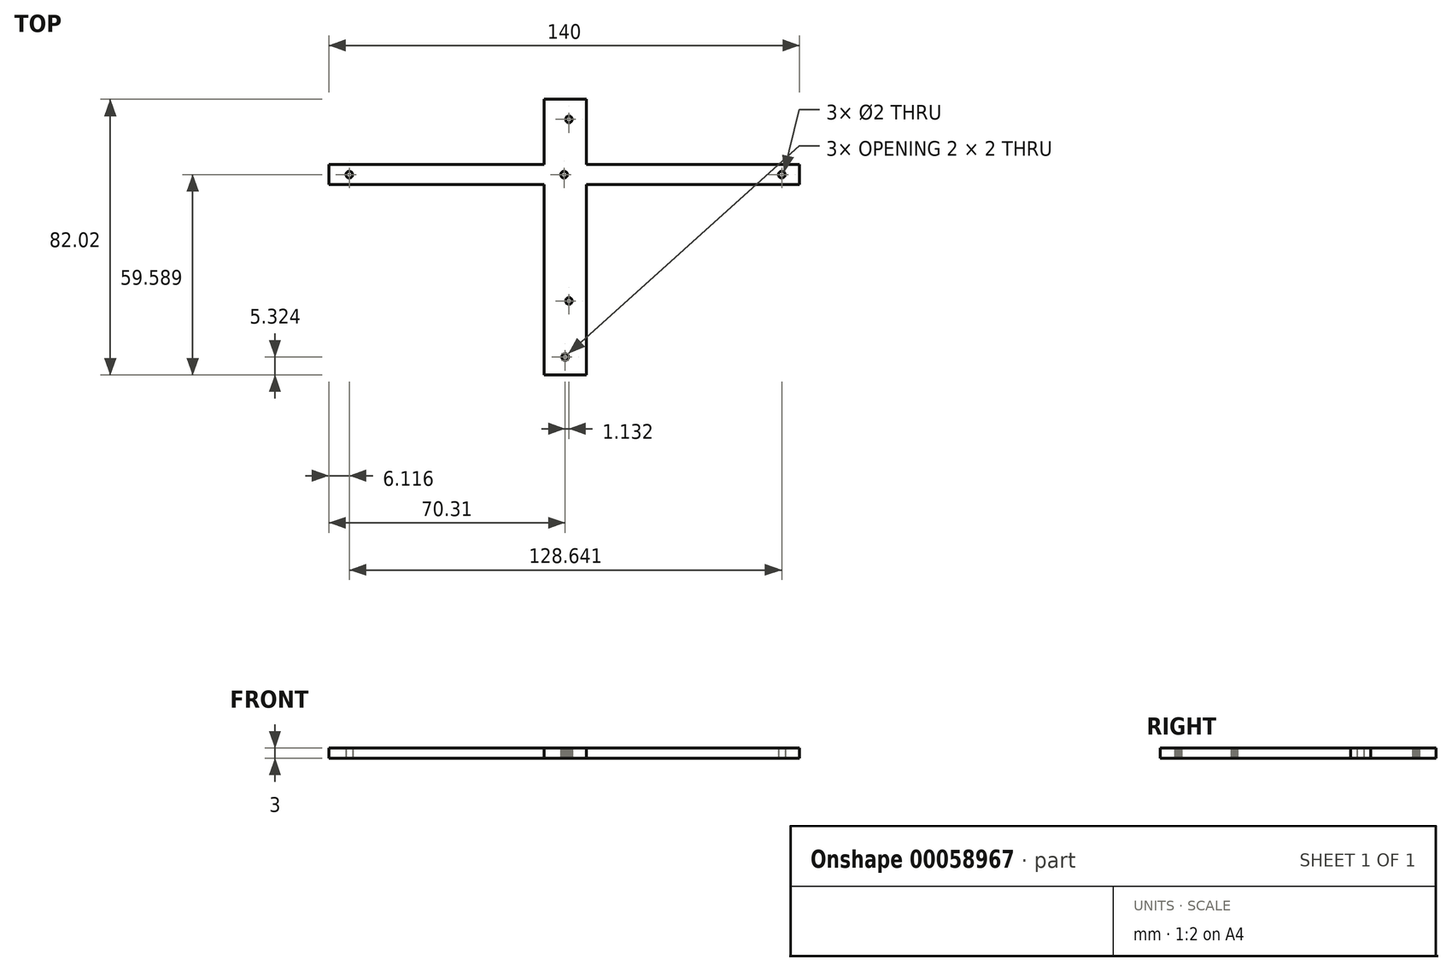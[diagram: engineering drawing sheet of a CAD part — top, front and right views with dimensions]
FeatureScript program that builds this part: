
annotation { "Feature Type Name" : "Feature", "Feature Type Description" : "" }
export const myFeature = defineFeature(function(context is Context, id is Id, definition is map)
    precondition{}
    {
        {
            var Q0;
            Q0=qCreatedBy(makeId("Top.planeOp"),FACE);
            var sketch = newSketch(context, id + "F0", { "sketchPlane" : qUnion([Q0])});
            skLineSegment(sketch, "E0", {"start": v(0.84, 33.8) * mm, "end": v(0.83, 33.92) * mm});
            skLineSegment(sketch, "E1", {"start": v(0.83, 33.92) * mm, "end": v(0.81, 34.04) * mm});
            skLineSegment(sketch, "E2", {"start": v(0.81, 34.04) * mm, "end": v(0.77, 34.16) * mm});
            skLineSegment(sketch, "E3", {"start": v(0.77, 34.16) * mm, "end": v(0.72, 34.28) * mm});
            skLineSegment(sketch, "E4", {"start": v(0.72, 34.28) * mm, "end": v(0.65, 34.38) * mm});
            skLineSegment(sketch, "E5", {"start": v(0.65, 34.38) * mm, "end": v(0.57, 34.48) * mm});
            skLineSegment(sketch, "E6", {"start": v(0.57, 34.48) * mm, "end": v(0.48, 34.57) * mm});
            skLineSegment(sketch, "E7", {"start": v(0.48, 34.57) * mm, "end": v(0.38, 34.64) * mm});
            skLineSegment(sketch, "E8", {"start": v(0.38, 34.64) * mm, "end": v(0.27, 34.7) * mm});
            skLineSegment(sketch, "E9", {"start": v(0.27, 34.7) * mm, "end": v(0.15, 34.75) * mm});
            skLineSegment(sketch, "E10", {"start": v(0.15, 34.75) * mm, "end": v(0.03, 34.78) * mm});
            skLineSegment(sketch, "E11", {"start": v(0.03, 34.78) * mm, "end": v(-0.1, 34.8) * mm});
            skLineSegment(sketch, "E12", {"start": v(-0.1, 34.8) * mm, "end": v(-0.22, 34.8) * mm});
            skLineSegment(sketch, "E13", {"start": v(-0.22, 34.8) * mm, "end": v(-0.35, 34.78) * mm});
            skLineSegment(sketch, "E14", {"start": v(-0.35, 34.78) * mm, "end": v(-0.47, 34.75) * mm});
            skLineSegment(sketch, "E15", {"start": v(-0.58, 34.7) * mm, "end": v(-0.7, 34.64) * mm});
            skLineSegment(sketch, "E16", {"start": v(-0.7, 34.64) * mm, "end": v(-0.8, 34.57) * mm});
            skLineSegment(sketch, "E17", {"start": v(-0.8, 34.57) * mm, "end": v(-0.89, 34.48) * mm});
            skLineSegment(sketch, "E18", {"start": v(-0.89, 34.48) * mm, "end": v(-0.97, 34.38) * mm});
            skLineSegment(sketch, "E19", {"start": v(-0.97, 34.38) * mm, "end": v(-1.03, 34.28) * mm});
            skLineSegment(sketch, "E20", {"start": v(-1.03, 34.28) * mm, "end": v(-1.09, 34.16) * mm});
            skLineSegment(sketch, "E21", {"start": v(-1.09, 34.16) * mm, "end": v(-1.13, 34.04) * mm});
            skLineSegment(sketch, "E22", {"start": v(-1.13, 34.04) * mm, "end": v(-1.15, 33.92) * mm});
            skLineSegment(sketch, "E23", {"start": v(-1.15, 33.92) * mm, "end": v(-1.16, 33.8) * mm});
            skLineSegment(sketch, "E24", {"start": v(-1.16, 33.8) * mm, "end": v(-1.15, 33.67) * mm});
            skLineSegment(sketch, "E25", {"start": v(-1.15, 33.67) * mm, "end": v(-1.13, 33.55) * mm});
            skLineSegment(sketch, "E26", {"start": v(-1.13, 33.55) * mm, "end": v(-1.09, 33.43) * mm});
            skLineSegment(sketch, "E27", {"start": v(-1.09, 33.43) * mm, "end": v(-1.03, 33.31) * mm});
            skLineSegment(sketch, "E28", {"start": v(-1.03, 33.31) * mm, "end": v(-0.97, 33.2) * mm});
            skLineSegment(sketch, "E29", {"start": v(-0.97, 33.2) * mm, "end": v(-0.89, 33.11) * mm});
            skLineSegment(sketch, "E30", {"start": v(-0.89, 33.11) * mm, "end": v(-0.8, 33.03) * mm});
            skLineSegment(sketch, "E31", {"start": v(-0.8, 33.03) * mm, "end": v(-0.7, 32.95) * mm});
            skLineSegment(sketch, "E32", {"start": v(-0.7, 32.95) * mm, "end": v(-0.58, 32.9) * mm});
            skLineSegment(sketch, "E33", {"start": v(-0.58, 32.9) * mm, "end": v(-0.47, 32.85) * mm});
            skLineSegment(sketch, "E34", {"start": v(-0.47, 32.85) * mm, "end": v(-0.35, 32.81) * mm});
            skLineSegment(sketch, "E35", {"start": v(-0.35, 32.81) * mm, "end": v(-0.22, 32.8) * mm});
            skLineSegment(sketch, "E36", {"start": v(-0.22, 32.8) * mm, "end": v(-0.1, 32.8) * mm});
            skLineSegment(sketch, "E37", {"start": v(-0.1, 32.8) * mm, "end": v(0.03, 32.81) * mm});
            skLineSegment(sketch, "E38", {"start": v(0.03, 32.81) * mm, "end": v(0.15, 32.85) * mm});
            skLineSegment(sketch, "E39", {"start": v(0.15, 32.85) * mm, "end": v(0.27, 32.9) * mm});
            skLineSegment(sketch, "E40", {"start": v(0.27, 32.9) * mm, "end": v(0.38, 32.95) * mm});
            skLineSegment(sketch, "E41", {"start": v(0.38, 32.95) * mm, "end": v(0.48, 33.03) * mm});
            skLineSegment(sketch, "E42", {"start": v(0.48, 33.03) * mm, "end": v(0.57, 33.11) * mm});
            skLineSegment(sketch, "E43", {"start": v(0.57, 33.11) * mm, "end": v(0.65, 33.2) * mm});
            skLineSegment(sketch, "E44", {"start": v(0.65, 33.2) * mm, "end": v(0.72, 33.31) * mm});
            skLineSegment(sketch, "E45", {"start": v(0.72, 33.31) * mm, "end": v(0.77, 33.43) * mm});
            skLineSegment(sketch, "E46", {"start": v(0.77, 33.43) * mm, "end": v(0.81, 33.55) * mm});
            skLineSegment(sketch, "E47", {"start": v(0.81, 33.55) * mm, "end": v(0.83, 33.67) * mm});
            skLineSegment(sketch, "E48", {"start": v(0.83, 33.67) * mm, "end": v(0.84, 33.8) * mm});
            skLineSegment(sketch, "E49", {"start": v(-0.29, -36.9) * mm, "end": v(-0.3, -36.78) * mm});
            skLineSegment(sketch, "E50", {"start": v(-0.3, -36.78) * mm, "end": v(-0.32, -36.66) * mm});
            skLineSegment(sketch, "E51", {"start": v(-0.32, -36.66) * mm, "end": v(-0.36, -36.54) * mm});
            skLineSegment(sketch, "E52", {"start": v(-0.36, -36.54) * mm, "end": v(-0.41, -36.42) * mm});
            skLineSegment(sketch, "E53", {"start": v(-0.41, -36.42) * mm, "end": v(-0.48, -36.32) * mm});
            skLineSegment(sketch, "E54", {"start": v(-0.48, -36.32) * mm, "end": v(-0.56, -36.22) * mm});
            skLineSegment(sketch, "E55", {"start": v(-0.56, -36.22) * mm, "end": v(-0.65, -36.14) * mm});
            skLineSegment(sketch, "E56", {"start": v(-0.65, -36.14) * mm, "end": v(-0.75, -36.06) * mm});
            skLineSegment(sketch, "E57", {"start": v(-0.75, -36.06) * mm, "end": v(-0.86, -36) * mm});
            skLineSegment(sketch, "E58", {"start": v(-0.86, -36) * mm, "end": v(-0.98, -35.95) * mm});
            skLineSegment(sketch, "E59", {"start": v(-0.98, -35.95) * mm, "end": v(-1.1, -35.92) * mm});
            skLineSegment(sketch, "E60", {"start": v(-1.1, -35.92) * mm, "end": v(-1.23, -35.9) * mm});
            skLineSegment(sketch, "E61", {"start": v(-1.23, -35.9) * mm, "end": v(-1.35, -35.9) * mm});
            skLineSegment(sketch, "E62", {"start": v(-1.35, -35.9) * mm, "end": v(-1.48, -35.92) * mm});
            skLineSegment(sketch, "E63", {"start": v(-1.48, -35.92) * mm, "end": v(-1.6, -35.95) * mm});
            skLineSegment(sketch, "E64", {"start": v(-1.6, -35.95) * mm, "end": v(-1.72, -36) * mm});
            skLineSegment(sketch, "E65", {"start": v(-1.72, -36) * mm, "end": v(-1.83, -36.06) * mm});
            skLineSegment(sketch, "E66", {"start": v(-1.83, -36.06) * mm, "end": v(-1.93, -36.14) * mm});
            skLineSegment(sketch, "E67", {"start": v(-1.93, -36.14) * mm, "end": v(-2.02, -36.22) * mm});
            skLineSegment(sketch, "E68", {"start": v(-2.02, -36.22) * mm, "end": v(-2.1, -36.32) * mm});
            skLineSegment(sketch, "E69", {"start": v(-2.1, -36.32) * mm, "end": v(-2.17, -36.42) * mm});
            skLineSegment(sketch, "E70", {"start": v(-2.17, -36.42) * mm, "end": v(-2.22, -36.54) * mm});
            skLineSegment(sketch, "E71", {"start": v(-2.22, -36.54) * mm, "end": v(-2.26, -36.66) * mm});
            skLineSegment(sketch, "E72", {"start": v(-2.26, -36.66) * mm, "end": v(-2.28, -36.78) * mm});
            skLineSegment(sketch, "E73", {"start": v(-2.28, -36.78) * mm, "end": v(-2.29, -36.9) * mm});
            skLineSegment(sketch, "E74", {"start": v(-2.29, -36.9) * mm, "end": v(-2.28, -37.03) * mm});
            skLineSegment(sketch, "E75", {"start": v(-2.28, -37.03) * mm, "end": v(-2.26, -37.15) * mm});
            skLineSegment(sketch, "E76", {"start": v(-2.26, -37.15) * mm, "end": v(-2.22, -37.27) * mm});
            skLineSegment(sketch, "E77", {"start": v(-2.22, -37.27) * mm, "end": v(-2.17, -37.39) * mm});
            skLineSegment(sketch, "E78", {"start": v(-2.17, -37.39) * mm, "end": v(-2.1, -37.5) * mm});
            skLineSegment(sketch, "E79", {"start": v(-2.1, -37.5) * mm, "end": v(-2.02, -37.6) * mm});
            skLineSegment(sketch, "E80", {"start": v(-2.02, -37.6) * mm, "end": v(-1.93, -37.68) * mm});
            skLineSegment(sketch, "E81", {"start": v(-1.93, -37.68) * mm, "end": v(-1.83, -37.75) * mm});
            skLineSegment(sketch, "E82", {"start": v(-1.83, -37.75) * mm, "end": v(-1.72, -37.81) * mm});
            skLineSegment(sketch, "E83", {"start": v(-1.72, -37.81) * mm, "end": v(-1.6, -37.86) * mm});
            skLineSegment(sketch, "E84", {"start": v(-1.6, -37.86) * mm, "end": v(-1.48, -37.89) * mm});
            skLineSegment(sketch, "E85", {"start": v(-1.48, -37.89) * mm, "end": v(-1.35, -37.9) * mm});
            skLineSegment(sketch, "E86", {"start": v(-1.35, -37.9) * mm, "end": v(-1.23, -37.9) * mm});
            skLineSegment(sketch, "E87", {"start": v(-1.23, -37.9) * mm, "end": v(-1.1, -37.89) * mm});
            skLineSegment(sketch, "E88", {"start": v(-1.1, -37.89) * mm, "end": v(-0.98, -37.86) * mm});
            skLineSegment(sketch, "E89", {"start": v(-0.98, -37.86) * mm, "end": v(-0.86, -37.81) * mm});
            skLineSegment(sketch, "E90", {"start": v(-0.86, -37.81) * mm, "end": v(-0.75, -37.75) * mm});
            skLineSegment(sketch, "E91", {"start": v(-0.75, -37.75) * mm, "end": v(-0.65, -37.68) * mm});
            skLineSegment(sketch, "E92", {"start": v(-0.65, -37.68) * mm, "end": v(-0.56, -37.6) * mm});
            skLineSegment(sketch, "E93", {"start": v(-0.56, -37.6) * mm, "end": v(-0.48, -37.5) * mm});
            skLineSegment(sketch, "E94", {"start": v(-0.48, -37.5) * mm, "end": v(-0.41, -37.39) * mm});
            skLineSegment(sketch, "E95", {"start": v(-0.41, -37.39) * mm, "end": v(-0.36, -37.27) * mm});
            skLineSegment(sketch, "E96", {"start": v(-0.36, -37.27) * mm, "end": v(-0.32, -37.15) * mm});
            skLineSegment(sketch, "E97", {"start": v(-0.32, -37.15) * mm, "end": v(-0.3, -37.03) * mm});
            skLineSegment(sketch, "E98", {"start": v(-0.3, -37.03) * mm, "end": v(-0.29, -36.9) * mm});
            skLineSegment(sketch, "E99", {"start": v(0.84, -20.2) * mm, "end": v(0.83, -20.08) * mm});
            skLineSegment(sketch, "E100", {"start": v(0.83, -20.08) * mm, "end": v(0.81, -19.96) * mm});
            skLineSegment(sketch, "E101", {"start": v(0.81, -19.96) * mm, "end": v(0.77, -19.84) * mm});
            skLineSegment(sketch, "E102", {"start": v(0.77, -19.84) * mm, "end": v(0.72, -19.72) * mm});
            skLineSegment(sketch, "E103", {"start": v(0.72, -19.72) * mm, "end": v(0.65, -19.62) * mm});
            skLineSegment(sketch, "E104", {"start": v(0.65, -19.62) * mm, "end": v(0.57, -19.52) * mm});
            skLineSegment(sketch, "E105", {"start": v(0.57, -19.52) * mm, "end": v(0.48, -19.43) * mm});
            skLineSegment(sketch, "E106", {"start": v(0.48, -19.43) * mm, "end": v(0.38, -19.36) * mm});
            skLineSegment(sketch, "E107", {"start": v(0.38, -19.36) * mm, "end": v(0.27, -19.3) * mm});
            skLineSegment(sketch, "E108", {"start": v(0.27, -19.3) * mm, "end": v(0.15, -19.25) * mm});
            skLineSegment(sketch, "E109", {"start": v(0.15, -19.25) * mm, "end": v(0.03, -19.22) * mm});
            skLineSegment(sketch, "E110", {"start": v(0.03, -19.22) * mm, "end": v(-0.1, -19.2) * mm});
            skLineSegment(sketch, "E111", {"start": v(-0.1, -19.2) * mm, "end": v(-0.22, -19.2) * mm});
            skLineSegment(sketch, "E112", {"start": v(-0.22, -19.2) * mm, "end": v(-0.35, -19.22) * mm});
            skLineSegment(sketch, "E113", {"start": v(-0.35, -19.22) * mm, "end": v(-0.47, -19.25) * mm});
            skLineSegment(sketch, "E114", {"start": v(-0.47, -19.25) * mm, "end": v(-0.58, -19.3) * mm});
            skLineSegment(sketch, "E115", {"start": v(-0.58, -19.3) * mm, "end": v(-0.7, -19.36) * mm});
            skLineSegment(sketch, "E116", {"start": v(-0.7, -19.36) * mm, "end": v(-0.8, -19.43) * mm});
            skLineSegment(sketch, "E117", {"start": v(-0.8, -19.43) * mm, "end": v(-0.89, -19.52) * mm});
            skLineSegment(sketch, "E118", {"start": v(-0.89, -19.52) * mm, "end": v(-0.97, -19.62) * mm});
            skLineSegment(sketch, "E119", {"start": v(-0.97, -19.62) * mm, "end": v(-1.03, -19.72) * mm});
            skLineSegment(sketch, "E120", {"start": v(-1.03, -19.72) * mm, "end": v(-1.09, -19.84) * mm});
            skLineSegment(sketch, "E121", {"start": v(-1.09, -19.84) * mm, "end": v(-1.13, -19.96) * mm});
            skLineSegment(sketch, "E122", {"start": v(-1.13, -19.96) * mm, "end": v(-1.15, -20.08) * mm});
            skLineSegment(sketch, "E123", {"start": v(-1.15, -20.08) * mm, "end": v(-1.16, -20.2) * mm});
            skLineSegment(sketch, "E124", {"start": v(-1.16, -20.2) * mm, "end": v(-1.15, -20.33) * mm});
            skLineSegment(sketch, "E125", {"start": v(-1.15, -20.33) * mm, "end": v(-1.13, -20.45) * mm});
            skLineSegment(sketch, "E126", {"start": v(-1.13, -20.45) * mm, "end": v(-1.09, -20.57) * mm});
            skLineSegment(sketch, "E127", {"start": v(-1.09, -20.57) * mm, "end": v(-1.03, -20.69) * mm});
            skLineSegment(sketch, "E128", {"start": v(-1.03, -20.69) * mm, "end": v(-0.97, -20.8) * mm});
            skLineSegment(sketch, "E129", {"start": v(-0.97, -20.8) * mm, "end": v(-0.89, -20.89) * mm});
            skLineSegment(sketch, "E130", {"start": v(-0.89, -20.89) * mm, "end": v(-0.8, -20.97) * mm});
            skLineSegment(sketch, "E131", {"start": v(-0.8, -20.97) * mm, "end": v(-0.7, -21.05) * mm});
            skLineSegment(sketch, "E132", {"start": v(-0.7, -21.05) * mm, "end": v(-0.58, -21.1) * mm});
            skLineSegment(sketch, "E133", {"start": v(-0.58, -21.1) * mm, "end": v(-0.47, -21.15) * mm});
            skLineSegment(sketch, "E134", {"start": v(-0.47, -21.15) * mm, "end": v(-0.35, -21.19) * mm});
            skLineSegment(sketch, "E135", {"start": v(-0.35, -21.19) * mm, "end": v(-0.22, -21.2) * mm});
            skLineSegment(sketch, "E136", {"start": v(-0.22, -21.2) * mm, "end": v(-0.1, -21.2) * mm});
            skLineSegment(sketch, "E137", {"start": v(-0.1, -21.2) * mm, "end": v(0.03, -21.19) * mm});
            skLineSegment(sketch, "E138", {"start": v(0.03, -21.19) * mm, "end": v(0.15, -21.15) * mm});
            skLineSegment(sketch, "E139", {"start": v(0.15, -21.15) * mm, "end": v(0.27, -21.1) * mm});
            skLineSegment(sketch, "E140", {"start": v(0.27, -21.1) * mm, "end": v(0.38, -21.05) * mm});
            skLineSegment(sketch, "E141", {"start": v(0.38, -21.05) * mm, "end": v(0.48, -20.97) * mm});
            skLineSegment(sketch, "E142", {"start": v(0.48, -20.97) * mm, "end": v(0.57, -20.89) * mm});
            skLineSegment(sketch, "E143", {"start": v(0.57, -20.89) * mm, "end": v(0.65, -20.8) * mm});
            skLineSegment(sketch, "E144", {"start": v(0.65, -20.8) * mm, "end": v(0.72, -20.69) * mm});
            skLineSegment(sketch, "E145", {"start": v(0.72, -20.69) * mm, "end": v(0.77, -20.57) * mm});
            skLineSegment(sketch, "E146", {"start": v(0.77, -20.57) * mm, "end": v(0.81, -20.45) * mm});
            skLineSegment(sketch, "E147", {"start": v(0.81, -20.45) * mm, "end": v(0.83, -20.33) * mm});
            skLineSegment(sketch, "E148", {"start": v(0.83, -20.33) * mm, "end": v(0.84, -20.2) * mm});
            skLineSegment(sketch, "E149", {"start": v(-0.47, 34.75) * mm, "end": v(-0.58, 34.7) * mm});
            skLineSegment(sketch, "E150", {"start": v(28.34, 33.8) * mm, "end": v(28.33, 33.92) * mm});
            skLineSegment(sketch, "E151", {"start": v(28.33, 33.92) * mm, "end": v(28.31, 34.04) * mm});
            skLineSegment(sketch, "E152", {"start": v(28.31, 34.04) * mm, "end": v(28.27, 34.16) * mm});
            skLineSegment(sketch, "E153", {"start": v(28.27, 34.16) * mm, "end": v(28.22, 34.28) * mm});
            skLineSegment(sketch, "E154", {"start": v(28.22, 34.28) * mm, "end": v(28.15, 34.38) * mm});
            skLineSegment(sketch, "E155", {"start": v(28.15, 34.38) * mm, "end": v(28.07, 34.48) * mm});
            skLineSegment(sketch, "E156", {"start": v(28.07, 34.48) * mm, "end": v(27.98, 34.57) * mm});
            skLineSegment(sketch, "E157", {"start": v(27.98, 34.57) * mm, "end": v(27.88, 34.64) * mm});
            skLineSegment(sketch, "E158", {"start": v(27.88, 34.64) * mm, "end": v(27.77, 34.7) * mm});
            skLineSegment(sketch, "E159", {"start": v(27.77, 34.7) * mm, "end": v(27.65, 34.75) * mm});
            skLineSegment(sketch, "E160", {"start": v(27.65, 34.75) * mm, "end": v(27.53, 34.78) * mm});
            skLineSegment(sketch, "E161", {"start": v(27.53, 34.78) * mm, "end": v(27.4, 34.8) * mm});
            skLineSegment(sketch, "E162", {"start": v(27.4, 34.8) * mm, "end": v(27.28, 34.8) * mm});
            skLineSegment(sketch, "E163", {"start": v(27.28, 34.8) * mm, "end": v(27.15, 34.78) * mm});
            skLineSegment(sketch, "E164", {"start": v(27.15, 34.78) * mm, "end": v(27.03, 34.75) * mm});
            skLineSegment(sketch, "E165", {"start": v(27.03, 34.75) * mm, "end": v(26.92, 34.7) * mm});
            skLineSegment(sketch, "E166", {"start": v(26.92, 34.7) * mm, "end": v(26.8, 34.64) * mm});
            skLineSegment(sketch, "E167", {"start": v(26.8, 34.64) * mm, "end": v(26.7, 34.57) * mm});
            skLineSegment(sketch, "E168", {"start": v(26.7, 34.57) * mm, "end": v(26.61, 34.48) * mm});
            skLineSegment(sketch, "E169", {"start": v(26.61, 34.48) * mm, "end": v(26.53, 34.38) * mm});
            skLineSegment(sketch, "E170", {"start": v(26.53, 34.38) * mm, "end": v(26.47, 34.28) * mm});
            skLineSegment(sketch, "E171", {"start": v(26.47, 34.28) * mm, "end": v(26.41, 34.16) * mm});
            skLineSegment(sketch, "E172", {"start": v(26.41, 34.16) * mm, "end": v(26.37, 34.04) * mm});
            skLineSegment(sketch, "E173", {"start": v(26.37, 34.04) * mm, "end": v(26.35, 33.92) * mm});
            skLineSegment(sketch, "E174", {"start": v(26.35, 33.92) * mm, "end": v(26.34, 33.8) * mm});
            skLineSegment(sketch, "E175", {"start": v(26.34, 33.8) * mm, "end": v(26.35, 33.67) * mm});
            skLineSegment(sketch, "E176", {"start": v(26.35, 33.67) * mm, "end": v(26.37, 33.55) * mm});
            skLineSegment(sketch, "E177", {"start": v(26.37, 33.55) * mm, "end": v(26.41, 33.43) * mm});
            skLineSegment(sketch, "E178", {"start": v(26.41, 33.43) * mm, "end": v(26.47, 33.31) * mm});
            skLineSegment(sketch, "E179", {"start": v(26.47, 33.31) * mm, "end": v(26.53, 33.2) * mm});
            skLineSegment(sketch, "E180", {"start": v(26.53, 33.2) * mm, "end": v(26.61, 33.11) * mm});
            skLineSegment(sketch, "E181", {"start": v(26.61, 33.11) * mm, "end": v(26.7, 33.03) * mm});
            skLineSegment(sketch, "E182", {"start": v(26.7, 33.03) * mm, "end": v(26.8, 32.95) * mm});
            skLineSegment(sketch, "E183", {"start": v(26.8, 32.95) * mm, "end": v(26.92, 32.9) * mm});
            skLineSegment(sketch, "E184", {"start": v(26.92, 32.9) * mm, "end": v(27.03, 32.85) * mm});
            skLineSegment(sketch, "E185", {"start": v(27.03, 32.85) * mm, "end": v(27.15, 32.81) * mm});
            skLineSegment(sketch, "E186", {"start": v(27.15, 32.81) * mm, "end": v(27.28, 32.8) * mm});
            skLineSegment(sketch, "E187", {"start": v(27.28, 32.8) * mm, "end": v(27.4, 32.8) * mm});
            skLineSegment(sketch, "E188", {"start": v(27.4, 32.8) * mm, "end": v(27.53, 32.81) * mm});
            skLineSegment(sketch, "E189", {"start": v(27.53, 32.81) * mm, "end": v(27.65, 32.85) * mm});
            skLineSegment(sketch, "E190", {"start": v(27.65, 32.85) * mm, "end": v(27.77, 32.9) * mm});
            skLineSegment(sketch, "E191", {"start": v(27.77, 32.9) * mm, "end": v(27.88, 32.95) * mm});
            skLineSegment(sketch, "E192", {"start": v(27.88, 32.95) * mm, "end": v(27.98, 33.03) * mm});
            skLineSegment(sketch, "E193", {"start": v(27.98, 33.03) * mm, "end": v(28.07, 33.11) * mm});
            skLineSegment(sketch, "E194", {"start": v(28.07, 33.11) * mm, "end": v(28.15, 33.2) * mm});
            skLineSegment(sketch, "E195", {"start": v(28.15, 33.2) * mm, "end": v(28.22, 33.31) * mm});
            skLineSegment(sketch, "E196", {"start": v(28.22, 33.31) * mm, "end": v(28.27, 33.43) * mm});
            skLineSegment(sketch, "E197", {"start": v(28.27, 33.43) * mm, "end": v(28.31, 33.55) * mm});
            skLineSegment(sketch, "E198", {"start": v(28.31, 33.55) * mm, "end": v(28.33, 33.67) * mm});
            skLineSegment(sketch, "E199", {"start": v(28.33, 33.67) * mm, "end": v(28.34, 33.8) * mm});
            skLineSegment(sketch, "E200", {"start": v(-2.29, -36.9) * mm, "end": v(-0.29, -36.9) * mm, "construction": true});
            skPoint(sketch, "E201", {"position": v(-1.29, -36.9) * mm});
            skLineSegment(sketch, "E202.bottom", {"start": v(-1.29, -42.23) * mm, "end": v(-7.55, -42.23) * mm});
            skLineSegment(sketch, "E202.top", {"start": v(-1.29, 39.79) * mm, "end": v(-7.55, 39.79) * mm});
            skLineSegment(sketch, "E202.right", {"start": v(-7.55, -42.23) * mm, "end": v(-7.55, 39.79) * mm});
            skPoint(sketch, "E203.oppositeSnap0", {"position": v(-4.42, -42.23) * mm});
            skLineSegment(sketch, "E203.bottom", {"start": v(-1.29, 39.79) * mm, "end": v(4.98, 39.79) * mm});
            skLineSegment(sketch, "E203.top", {"start": v(-1.29, -42.23) * mm, "end": v(4.98, -42.23) * mm});
            skLineSegment(sketch, "E203.right", {"start": v(4.98, 28.88) * mm, "end": v(4.98, -42.23) * mm});
            skLineSegment(sketch, "E204.bottom", {"start": v(34.68, 39.79) * mm, "end": v(4.98, 39.79) * mm});
            skLineSegment(sketch, "E204.top", {"start": v(34.68, 28.88) * mm, "end": v(4.98, 28.88) * mm});
            skLineSegment(sketch, "E204.left", {"start": v(34.68, 39.79) * mm, "end": v(34.68, 28.88) * mm});
            skPoint(sketch, "E205", {"position": v(-1.6, 17.36) * mm});
            skLineSegment(sketch, "E206.bottom", {"start": v(-1.6, 20.36) * mm, "end": v(-71.6, 20.36) * mm});
            skLineSegment(sketch, "E206.top", {"start": v(-1.6, 14.36) * mm, "end": v(-71.6, 14.36) * mm});
            skLineSegment(sketch, "E206.left", {"start": v(-1.6, 20.36) * mm, "end": v(-1.6, 14.36) * mm});
            skLineSegment(sketch, "E206.right", {"start": v(-71.6, 20.36) * mm, "end": v(-71.6, 14.36) * mm});
            skLineSegment(sketch, "E207.bottom", {"start": v(-1.6, 20.36) * mm, "end": v(68.4, 20.36) * mm});
            skLineSegment(sketch, "E207.top", {"start": v(-1.6, 14.36) * mm, "end": v(68.4, 14.36) * mm});
            skLineSegment(sketch, "E207.right", {"start": v(68.4, 20.36) * mm, "end": v(68.4, 14.36) * mm});
            skLineSegment(sketch, "E208", {"start": v(4.98, 39.79) * mm, "end": v(4.98, 28.88) * mm});
            skLineSegment(sketch, "E209", {"start": v(-71.6, 17.36) * mm, "end": v(68.4, 17.36) * mm, "construction": true});
            skCircle(sketch, "E210", {"center": v(63.16, 17.36) * mm, "radius": 1 * mm});
            skCircle(sketch, "E211", {"center": v(-65.48, 17.36) * mm, "radius": 1 * mm});
            skLineSegment(sketch, "E212", {"start": v(-1.16, 33.8) * mm, "end": v(0.84, 33.8) * mm, "construction": true});
            skPoint(sketch, "E213", {"position": v(-0.16, 33.8) * mm});
            skLineSegment(sketch, "E214.bottom", {"start": v(-7.55, 39.79) * mm, "end": v(4.98, 39.79) * mm});
            skLineSegment(sketch, "E214.top", {"start": v(-7.55, 99.79) * mm, "end": v(4.98, 99.79) * mm});
            skLineSegment(sketch, "E214.left", {"start": v(-7.55, 39.79) * mm, "end": v(-7.55, 99.79) * mm});
            skLineSegment(sketch, "E214.right", {"start": v(4.98, 39.79) * mm, "end": v(4.98, 99.79) * mm});
            skCircle(sketch, "E215", {"center": v(-1.29, 94.79) * mm, "radius": 1.5 * mm});
            skPoint(sketch, "E215.centerSnap0", {"position": v(-1.29, 99.79) * mm});
            skLineSegment(sketch, "E216.bottom", {"start": v(-21.29, 99.79) * mm, "end": v(18.71, 99.79) * mm});
            skLineSegment(sketch, "E216.top", {"start": v(-21.29, 94.79) * mm, "end": v(18.71, 94.79) * mm});
            skLineSegment(sketch, "E216.left", {"start": v(-21.29, 99.79) * mm, "end": v(-21.29, 94.79) * mm});
            skLineSegment(sketch, "E216.right", {"start": v(18.71, 99.79) * mm, "end": v(18.71, 94.79) * mm});
            skCircle(sketch, "E217", {"center": v(-16.29, 97.29) * mm, "radius": 1 * mm});
            skPoint(sketch, "E217.centerSnap0", {"position": v(-21.29, 97.29) * mm});
            skCircle(sketch, "E218", {"center": v(13.71, 97.29) * mm, "radius": 1 * mm});
            skPoint(sketch, "E218.centerSnap0", {"position": v(18.71, 97.29) * mm});
            skCircle(sketch, "E219", {"center": v(-1.6, 17.36) * mm, "radius": 1 * mm});
            skSolve(sketch);
        }
        {
            var Q0;
            Q0=makeQuery(id+"F0.imprint","IMPRINT",FACE,{"disambiguationData":[TD([[makeQuery(id+"F0.imprint","IMPRINT",EDGE,{"derivedFrom":sQuery(id+"F0.wireOp",EDGE,"E49")}),-1.0]])]});
            var Q1;
            {var subQ0=sQuery(id+"F0.wireOp",EDGE,"d9d795a4-12a4-42d5-b6af-be746a3b56d2");Q1=makeQuery(id+"F0.imprint","IMPRINT",FACE,{"disambiguationData":[TD([[makeQuery(id+"F0.imprint","IMPRINT",EDGE,{"derivedFrom":subQ0}),-1.0]])]});}
            var Q2;
            Q2=makeQuery(id+"F0.imprint","IMPRINT",FACE,{"disambiguationData":[TD([[makeQuery(id+"F0.imprint","IMPRINT",EDGE,{"derivedFrom":sQuery(id+"F0.wireOp",EDGE,"044ca1f0-f9e8-4e3d-8bcb-43c99246160e")}),-1.0]])]});
            var Q3;
            Q3=makeQuery(id+"F0.imprint","IMPRINT",FACE,{"disambiguationData":[TD([[makeQuery(id+"F0.imprint","IMPRINT",EDGE,{"derivedFrom":sQuery(id+"F0.wireOp",EDGE,"E0")}),-1.0]])]});
            var Q4;
            {var subQ5=sQuery(id+"F0.wireOp",EDGE,"E206.right");Q4=makeQuery(id+"F0.imprint","IMPRINT",FACE,{"disambiguationData":[TD([[makeQuery(id+"F0.imprint","IMPRINT",EDGE,{"derivedFrom":subQ5}),1.0]])]});}
            var Q5;
            {var subQ5=sQuery(id+"F0.wireOp",EDGE,"E207.right");Q5=makeQuery(id+"F0.imprint","IMPRINT",FACE,{"disambiguationData":[TD([[makeQuery(id+"F0.imprint","IMPRINT",EDGE,{"derivedFrom":subQ5}),-1.0]])]});}
            var Q6;
            {var subQ4=sQuery(id+"F0.wireOp",EDGE,"E206.top");var subQ6=sQuery(id+"F0.wireOp",EDGE,"E202.right");var subQ7=makeQuery(id+"F0.imprint","INTERSECT",VERTEX,{"derivedFrom":[subQ6,subQ4]});Q6=makeQuery(id+"F0.imprint","IMPRINT",FACE,{"disambiguationData":[TD([[makeQuery(id+"F0.imprint","IMPRINT",EDGE,{"disambiguationData":[TD([[subQ7,-1.0]])],"derivedFrom":subQ6}),-1.0]])]});}
            var Q7;
            {var subQ3=sQuery(id+"F0.wireOp",EDGE,"E203.right");var subQ5=sQuery(id+"F0.wireOp",EDGE,"E207.bottom");var subQ7=makeQuery(id+"F0.imprint","INTERSECT",VERTEX,{"derivedFrom":[subQ3,subQ5]});Q7=makeQuery(id+"F0.imprint","IMPRINT",FACE,{"disambiguationData":[TD([[makeQuery(id+"F0.imprint","IMPRINT",EDGE,{"disambiguationData":[TD([[subQ7,-1.0]])],"derivedFrom":subQ3}),-1.0]])]});}
            extrude(context, id + "F1", {"entities" : qUnion([Q0, Q1, Q2, Q3, Q4, Q5, Q6, Q7]), "depth" : 3 * mm});
        }
    });
